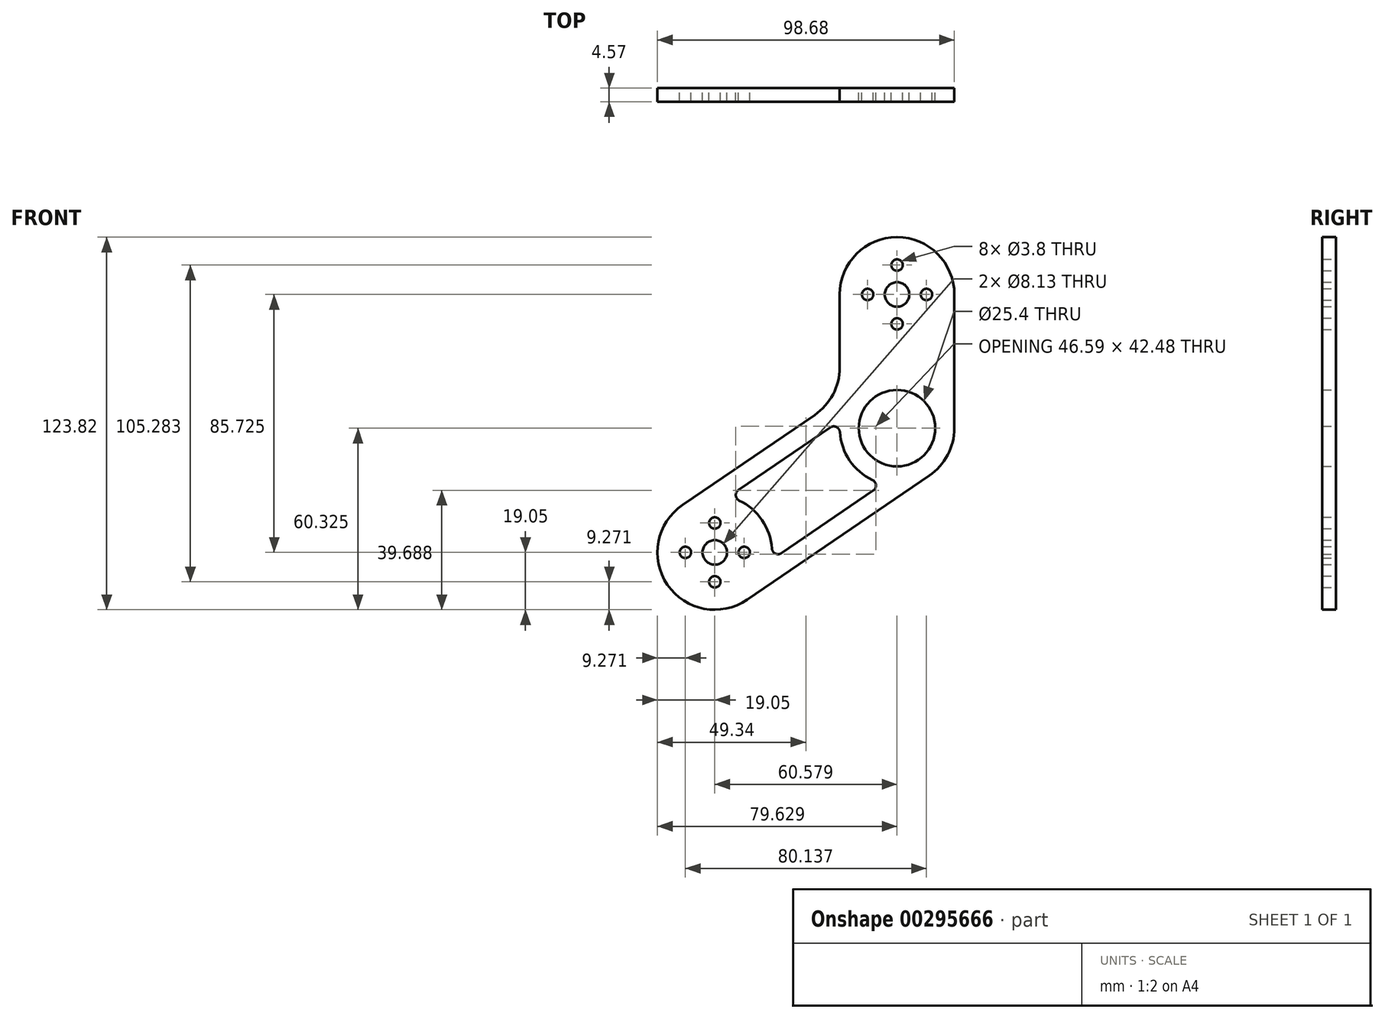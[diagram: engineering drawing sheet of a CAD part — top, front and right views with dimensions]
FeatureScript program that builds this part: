
annotation { "Feature Type Name" : "Feature", "Feature Type Description" : "" }
export const myFeature = defineFeature(function(context is Context, id is Id, definition is map)
    precondition{}
    {
        {
            var Q0;
            Q0=qCreatedBy(makeId("Front.planeOp"),FACE);
            var sketch = newSketch(context, id + "F0", { "sketchPlane" : qUnion([Q0])});
            skCircle(sketch, "E0", {"center": v(0, 0) * mm, "radius": 4.06 * mm});
            skCircle(sketch, "E1", {"center": v(0, 9.78) * mm, "radius": 1.9 * mm});
            skCircle(sketch, "E2.MirrorC", {"center": v(0, -9.78) * mm, "radius": 1.9 * mm});
            skCircle(sketch, "E3", {"center": v(0, 0) * mm, "radius": 9.78 * mm, "construction": true});
            skCircle(sketch, "E4", {"center": v(-9.78, 0) * mm, "radius": 1.9 * mm});
            skCircle(sketch, "E5.MirrorC", {"center": v(9.78, 0) * mm, "radius": 1.9 * mm});
            skCircle(sketch, "E6", {"center": v(0, 0) * mm, "radius": 19.05 * mm, "construction": true});
            skPoint(sketch, "E7", {"position": v(60.58, 0) * mm});
            skPoint(sketch, "E8", {"position": v(60.58, 41.28) * mm});
            skCircle(sketch, "E9", {"center": v(60.58, 41.28) * mm, "radius": 19.05 * mm, "construction": true});
            skLineSegment(sketch, "E10", {"start": v(-10.73, 15.74) * mm, "end": v(49.85, 57.02) * mm, "construction": true});
            skLineSegment(sketch, "E11", {"start": v(10.73, -15.74) * mm, "end": v(71.3, 25.53) * mm});
            skArc(sketch, "E12", {"start": v(10.73, -15.74) * mm, "mid": v(-15.74, -10.73) * mm, "end": v(-10.73, 15.74) * mm});
            skPoint(sketch, "E13", {"position": v(60.58, 85.73) * mm});
            skCircle(sketch, "E14", {"center": v(60.58, 85.73) * mm, "radius": 19.05 * mm, "construction": true});
            skLineSegment(sketch, "E15", {"start": v(41.53, 85.73) * mm, "end": v(41.53, 41.28) * mm, "construction": true});
            skLineSegment(sketch, "E16", {"start": v(79.63, 85.73) * mm, "end": v(79.63, 41.28) * mm});
            skArc(sketch, "E17", {"start": v(71.3, 25.53) * mm, "mid": v(77.42, 32.37) * mm, "end": v(79.63, 41.28) * mm});
            skArc(sketch, "E18", {"start": v(79.63, 85.73) * mm, "mid": v(60.58, 104.78) * mm, "end": v(41.53, 85.73) * mm});
            skArc(sketch, "E19", {"start": v(33.2, 45.68) * mm, "mid": v(39.32, 52.51) * mm, "end": v(41.53, 61.42) * mm});
            skLineSegment(sketch, "E20", {"start": v(41.53, 61.42) * mm, "end": v(41.53, 85.73) * mm});
            skLineSegment(sketch, "E21", {"start": v(33.2, 45.68) * mm, "end": v(-10.73, 15.74) * mm});
            skCircle(sketch, "E22", {"center": v(60.58, 85.73) * mm, "radius": 4.06 * mm});
            skCircle(sketch, "E23", {"center": v(60.58, 85.73) * mm, "radius": 9.78 * mm, "construction": true});
            skCircle(sketch, "E24", {"center": v(60.58, 95.5) * mm, "radius": 1.9 * mm});
            skLineSegment(sketch, "E25", {"start": v(41.53, 85.73) * mm, "end": v(79.63, 85.73) * mm, "construction": true});
            skLineSegment(sketch, "E26", {"start": v(60.58, 104.78) * mm, "end": v(60.58, 66.68) * mm, "construction": true});
            skCircle(sketch, "E27.MirrorC", {"center": v(60.58, 75.95) * mm, "radius": 1.9 * mm});
            skCircle(sketch, "E28", {"center": v(50.8, 85.73) * mm, "radius": 1.9 * mm});
            skCircle(sketch, "E29.MirrorC", {"center": v(70.36, 85.73) * mm, "radius": 1.9 * mm});
            skArc(sketch, "E30", {"start": v(-10.73, 15.74) * mm, "mid": v(15.74, 10.73) * mm, "end": v(10.73, -15.74) * mm, "construction": true});
            skLineSegment(sketch, "E31", {"start": v(4.58, 18.5) * mm, "end": v(41.7, 43.78) * mm, "construction": true});
            skLineSegment(sketch, "E32", {"start": v(18.89, -2.5) * mm, "end": v(56, 22.78) * mm, "construction": true});
            skArc(sketch, "E33", {"start": v(38.4, 41.53) * mm, "mid": v(40.43, 41.68) * mm, "end": v(41.57, 39.99) * mm});
            skArc(sketch, "E34", {"start": v(52.43, 24.06) * mm, "mid": v(53.58, 22.38) * mm, "end": v(52.7, 20.54) * mm});
            skArc(sketch, "E35", {"start": v(22.18, -0.26) * mm, "mid": v(20.15, -0.4) * mm, "end": v(19, 1.29) * mm});
            skArc(sketch, "E36", {"start": v(8.15, 17.22) * mm, "mid": v(7, 18.9) * mm, "end": v(7.88, 20.73) * mm});
            skLineSegment(sketch, "E37", {"start": v(7.88, 20.73) * mm, "end": v(38.4, 41.53) * mm});
            skLineSegment(sketch, "E38", {"start": v(52.7, 20.54) * mm, "end": v(22.18, -0.26) * mm});
            skArc(sketch, "E39", {"start": v(8.15, 17.22) * mm, "mid": v(15.74, 10.73) * mm, "end": v(19, 1.29) * mm});
            skArc(sketch, "E40", {"start": v(41.57, 39.99) * mm, "mid": v(44.84, 30.55) * mm, "end": v(52.43, 24.06) * mm});
            skCircle(sketch, "E41", {"center": v(60.58, 41.28) * mm, "radius": 12.7 * mm});
            skSolve(sketch);
        }
        {
            var Q0;
            Q0=makeQuery(id+"F0.imprint","IMPRINT",FACE,{"disambiguationData":[TD([[makeQuery(id+"F0.imprint","IMPRINT",EDGE,{"derivedFrom":sQuery(id+"F0.wireOp",EDGE,"E0")}),-1.0]])]});
            extrude(context, id + "F1", {"entities" : qUnion([Q0]), "depth" : 4.57 * mm});
        }
    });
